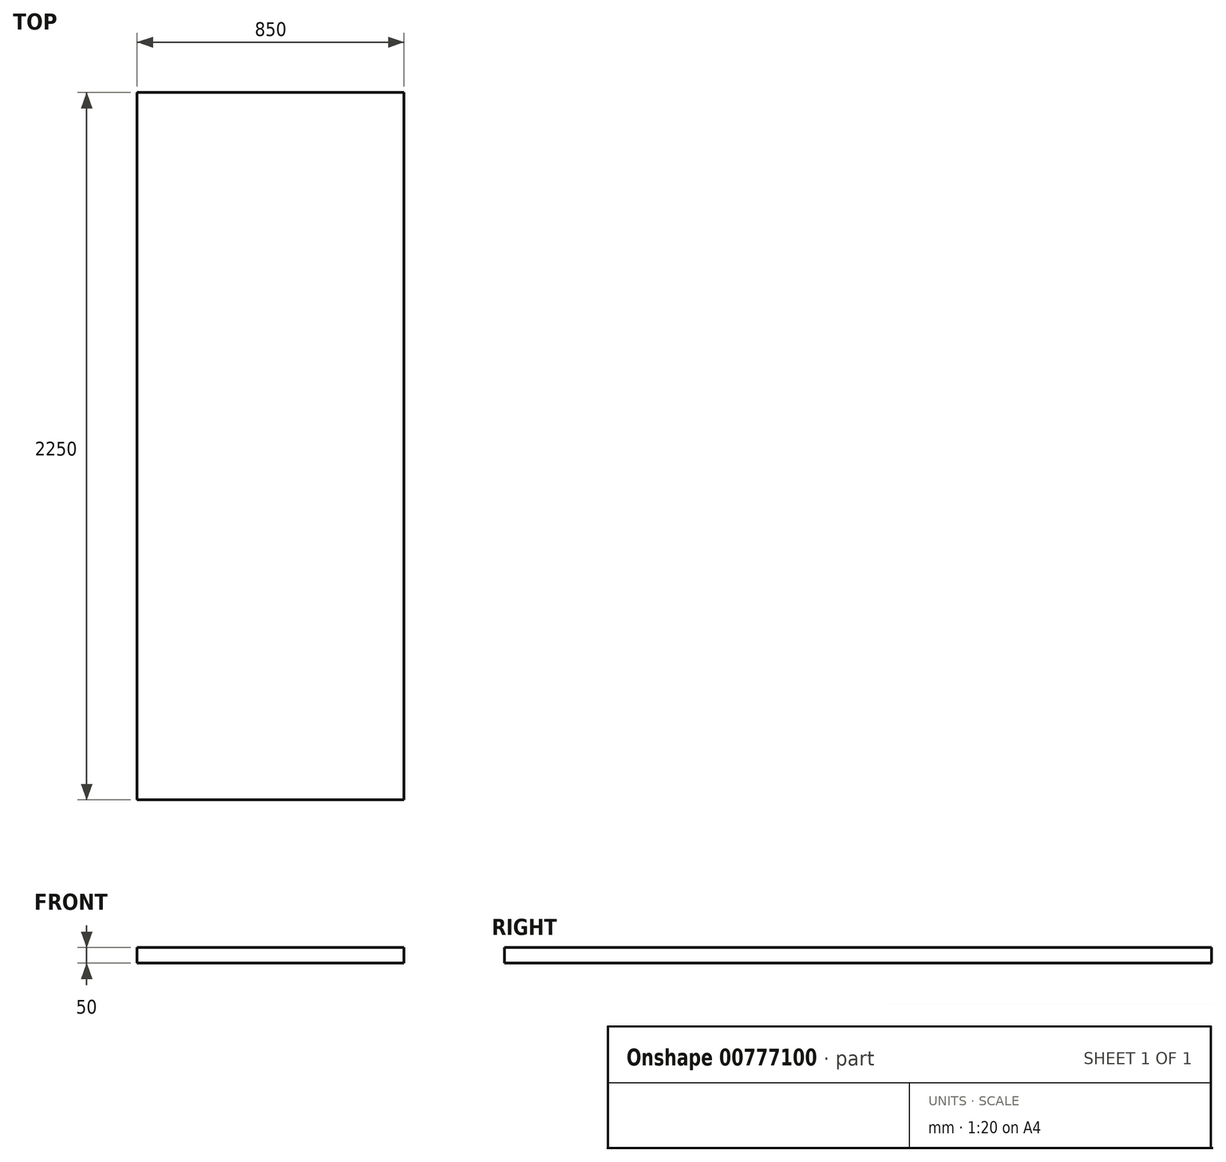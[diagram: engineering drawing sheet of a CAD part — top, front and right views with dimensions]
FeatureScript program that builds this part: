
annotation { "Feature Type Name" : "Feature", "Feature Type Description" : "" }
export const myFeature = defineFeature(function(context is Context, id is Id, definition is map)
    precondition{}
    {
        {
            var Q0;
            Q0=qCreatedBy(makeId("Front.planeOp"),FACE);
            var sketch = newSketch(context, id + "F0", { "sketchPlane" : qUnion([Q0])});
            skLineSegment(sketch, "E0.bottom", {"start": v(0, 0) * mm, "end": v(-850, 0) * mm});
            skLineSegment(sketch, "E0.top", {"start": v(0, 50) * mm, "end": v(-850, 50) * mm});
            skLineSegment(sketch, "E0.left", {"start": v(0, 0) * mm, "end": v(0, 50) * mm});
            skLineSegment(sketch, "E0.right", {"start": v(-850, 0) * mm, "end": v(-850, 50) * mm});
            skSolve(sketch);
        }
        {
            var Q0;
            Q0 = qSketchRegion(id + "F0", true);
            extrude(context, id + "F1", {"entities" : qUnion([Q0]), "depth" : 2250 * mm, "offsetDistance" : 25 * mm});
        }
    });
